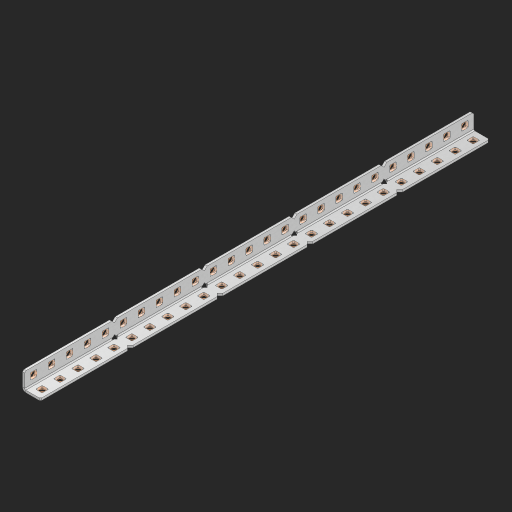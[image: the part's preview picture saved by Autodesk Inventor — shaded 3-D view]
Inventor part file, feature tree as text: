
AUTODESK INVENTOR PART (.ipt)
format: ipt  version: 2023 (Build 270158000, 158)  size: 902,656 bytes
history: native  units: in
note: dims shown in document units (in); Inventor stores cm internally (conversion verified against a paired STEP export)
features: other x56, extrude x51, sheet_metal_op x8, sketch x5, pattern_linear x1, mirror x1, chamfer x1
ambient origin geometry x8: Origin, YZ Plane, XZ Plane, XY Plane, X Axis, Y Axis, Z Axis, Center Point
bodies: Solid1 (feature_tree), Body (feature_tree)
feature tree (123):
  sheet_metal_op  "Flanges"
  sheet_metal_op  "Body Pattern"
  other  "Arc Length"
  pattern_linear  "Notch Pattern"  Spacing1=0.125in  [1 undecoded]
  other  "Diagonal Plane"
  mirror  "Everything Mirrored"
  chamfer  "End Chamfer"
  sketch  "Sketch1"  dims[d0=0.5in]
  other  "Plate1"
  sketch  "Sketch2"  dims[d1=12.5in]
  other  "Plate2"
  sheet_metal_op  "Bend1"
  sheet_metal_op  "Corner1"
  sketch  "Sketch8"  dims[d2=0.0625in]
  sketch  "Sketch9"  dims[d3=0.0625in]
  other  "Srf91"
  sheet_metal_op  "Body Pattern Sketch"
  other  "Srf92"
  sketch  "Sketch13"  dims[d4=0.0312in d5=0.125in d6=0.0625in d7=0.5in d8=90.0deg d9=0.0312in d10=0.25in d11=0.0625in d12=0.0625in d49=0.182in d50=0.02in d52=0.25in d53=0.0625in d54=0.0in d55=0.172in d56=1.0in d57=0.0in d85=0.1473in d86=0.1782in d89=0.0625in d90=0.0in d91=0.04in d92=0.0491in d95=2.5in d96=0.04in d97=0.25in d98=45.0deg d123=0.204in d126=0.0491in d127=0.1473in d128=0.08in d129=0.04in d130=2.5in d131=9.8425in d133=0.5in d134=0.3937in d136=1.0in]
  other  "Srf856"
  other  "Srf857"
  other  "Srf858"
  other  "Srf859"
  other  "Srf860"
  other  "Srf861"
  other  "Srf1275"
  other  "Srf1276"
  other  "Srf1278"
  other  "Srf1279"
  other  "Srf1280"
  other  "Srf1281"
  other  "Srf1282"
  other  "Srf1283"
  other  "Srf1383"
  other  "Srf1384"
  other  "Srf1385"
  other  "Srf1386"
  other  "Srf1387"
  other  "Srf1388"
  other  "Srf1389"
  other  "Srf1390"
  other  "Srf1391"
  other  "Srf1392"
  other  "Srf1393"
  other  "Srf1394"
  other  "Srf1395"
  other  "Srf1396"
  other  "Srf1397"
  other  "Srf1398"
  other  "Srf1399"
  other  "Srf1400"
  other  "Srf1475"
  other  "Srf1476"
  other  "Srf1477"
  other  "Srf1478"
  other  "Srf1479"
  other  "Srf1480"
  other  "Srf1481"
  other  "Srf1482"
  other  "Srf1483"
  other  "Srf1484"
  other  "Srf1485"
  other  "Srf1486"
  other  "Srf1487"
  other  "Srf1488"
  other  "Srf1489"
  other  "Srf1490"
  other  "Srf1491"
  other  "Srf1492"
  sheet_metal_op  "Body Stamp"
  sheet_metal_op  "Body Circle"
  sheet_metal_op  "Notch"
  extrude  "ExtrusionSrf92"  Depth=0.0625in
  extrude  "ExtrusionSrf856"  Depth=0.5in TaperAngle=90.0deg
  extrude  "ExtrusionSrf857"  Depth=0.25in
  extrude  "ExtrusionSrf858"  Depth=0.0625in
  extrude  "ExtrusionSrf859"  Depth=0.0625in
  extrude  "ExtrusionSrf860"  Depth=0.3937in
  extrude  "ExtrusionSrf861"  Depth=0.02in
  extrude  "ExtrusionSrf1275"  Depth=0.25in
  extrude  "ExtrusionSrf1276"  Depth=0.0625in
  extrude  "ExtrusionSrf1277"  TaperAngle=0.0deg  [1 undecoded]
  extrude  "ExtrusionSrf1278"  Depth=0.3937in
  extrude  "ExtrusionSrf1279"  Depth=0.3937in TaperAngle=0.0deg
  extrude  "ExtrusionSrf1280"  Depth=0.3937in
  extrude  "ExtrusionSrf1281"  Depth=0.3937in
  extrude  "ExtrusionSrf1282"  Depth=0.0625in
  extrude  "ExtrusionSrf1383"  Depth=0.3937in TaperAngle=0.0deg
  extrude  "ExtrusionSrf1384"  Depth=0.3937in
  extrude  "ExtrusionSrf1385"  Depth=0.25in TaperAngle=45.0deg
  extrude  "ExtrusionSrf1386"  Depth=0.3937in
  extrude  "ExtrusionSrf1387"  Depth=0.3937in
  extrude  "ExtrusionSrf1388"  Depth=0.3937in
  extrude  "ExtrusionSrf1389"  Depth=0.3937in
  extrude  "ExtrusionSrf1390"  Depth=0.3937in
  extrude  "ExtrusionSrf1391"  Depth=0.3937in
  extrude  "ExtrusionSrf1392"  Depth=0.3937in
  extrude  "ExtrusionSrf1393"  Depth=0.5in
  extrude  "ExtrusionSrf1394"  [1 undecoded]
  extrude  "ExtrusionSrf1395"  [1 undecoded]
  extrude  "ExtrusionSrf1396"  [1 undecoded]
  extrude  "ExtrusionSrf1397"  [1 undecoded]
  extrude  "ExtrusionSrf1398"  [1 undecoded]
  extrude  "ExtrusionSrf1399"  [1 undecoded]
  extrude  "ExtrusionSrf1400"  [1 undecoded]
  extrude  "ExtrusionSrf1475"  [1 undecoded]
  extrude  "ExtrusionSrf1476"  [1 undecoded]
  extrude  "ExtrusionSrf1477"  [1 undecoded]
  extrude  "ExtrusionSrf1478"  [1 undecoded]
  extrude  "ExtrusionSrf1479"  [1 undecoded]
  extrude  "ExtrusionSrf1480"  [1 undecoded]
  extrude  "ExtrusionSrf1481"  [1 undecoded]
  extrude  "ExtrusionSrf1482"  [1 undecoded]
  extrude  "ExtrusionSrf1483"  [1 undecoded]
  extrude  "ExtrusionSrf1484"  [1 undecoded]
  extrude  "ExtrusionSrf1485"  [1 undecoded]
  extrude  "ExtrusionSrf1486"  [1 undecoded]
  extrude  "ExtrusionSrf1487"  [1 undecoded]
  extrude  "ExtrusionSrf1488"  [1 undecoded]
  extrude  "ExtrusionSrf1489"  [1 undecoded]
  extrude  "ExtrusionSrf1490"  [1 undecoded]
  extrude  "ExtrusionSrf1491"  [1 undecoded]
  extrude  "ExtrusionSrf1492"  [1 undecoded]
note: 27 required parameter values undecoded (feature->parameter linkage not recoverable at this tier; creation-order binding heuristic only, values carry confidence <= 0.55)
